FCSTD DOCUMENT  (FreeCAD 0.17R9910 (Git))
Label: housing
License: All rights reserved
LicenseURL: http://en.wikipedia.org/wiki/All_rights_reserved
objects: Sketcher::SketchObject×1, PartDesign::Body×1, App::Part×1
note: 2 computed .brp shape members not serialized (recipe doc carries the construction recipe); baked Part::Feature solids carry a one-line shape summary decoded from their .brp

FEATURE [Sketcher::SketchObject] Sketch
  MapMode = 5
  Support = -> [XY_Plane001]
  sketch-geometry (22):
    g0: LineSegment StartX=0 StartY=42 StartZ=0 EndX=26 EndY=42 EndZ=0
    g1: LineSegment StartX=26 StartY=42 StartZ=0 EndX=34 EndY=42 EndZ=0
    g2: LineSegment StartX=34 StartY=42 StartZ=0 EndX=34 EndY=50 EndZ=0
    g3: LineSegment StartX=34 StartY=50 StartZ=0 EndX=39 EndY=55 EndZ=0
    g4: LineSegment StartX=39 StartY=55 StartZ=0 EndX=55 EndY=55 EndZ=0
    g5: LineSegment StartX=55 StartY=55 StartZ=0 EndX=60 EndY=50 EndZ=0
    g6: LineSegment StartX=60 StartY=50 StartZ=0 EndX=60 EndY=42 EndZ=0
    g7: LineSegment StartX=60 StartY=42 StartZ=0 EndX=68 EndY=42 EndZ=0
    g8: LineSegment StartX=68 StartY=0 StartZ=0 EndX=60 EndY=0 EndZ=0
    g9: LineSegment StartX=60 StartY=0 StartZ=0 EndX=34 EndY=0 EndZ=0
    g10: LineSegment StartX=34 StartY=0 StartZ=0 EndX=26 EndY=0 EndZ=0
    g11: LineSegment StartX=26 StartY=0 StartZ=0 EndX=0 EndY=0 EndZ=0
    g12: LineSegment [constr] StartX=0 StartY=0 StartZ=0 EndX=0 EndY=42 EndZ=0
    g13: LineSegment [constr] StartX=34 StartY=42 StartZ=0 EndX=60 EndY=42 EndZ=0
    g14: LineSegment [constr] StartX=26 StartY=42 StartZ=0 EndX=26 EndY=0 EndZ=0
    g15: LineSegment [constr] StartX=34 StartY=0 StartZ=0 EndX=34 EndY=42 EndZ=0
    g16: LineSegment [constr] StartX=60 StartY=42 StartZ=0 EndX=60 EndY=0 EndZ=0
    g17: LineSegment [constr] StartX=34 StartY=50 StartZ=0 EndX=60 EndY=50 EndZ=0
    g18: LineSegment StartX=68 StartY=42 StartZ=0 EndX=68 EndY=0 EndZ=0
    g19: LineSegment StartX=0 StartY=42 StartZ=0 EndX=-5 EndY=37 EndZ=0
    g20: LineSegment StartX=-5 StartY=37 StartZ=0 EndX=-5 EndY=5 EndZ=0
    g21: LineSegment StartX=-5 StartY=5 StartZ=0 EndX=0 EndY=0 EndZ=0
  constraints (59):
    c: Horizontal(g0)
    c: Coincident(g0,g1)
    c: Horizontal(g1)
    c: Coincident(g1,g2)
    c: Vertical(g2)
    c: Coincident(g2,g3)
    c: Coincident(g3,g4)
    c: Horizontal(g4)
    c: Coincident(g4,g5)
    c: Coincident(g5,g6)
    c: Vertical(g6)
    c: Coincident(g6,g7)
    c: Coincident(g8,g9)
    c: Horizontal(g9)
    c: Coincident(g9,g10)
    c: Coincident(g10,g11)
    c: Horizontal(g11)
    c: Coincident(g11,g12)
    c: Coincident(g12,g0)
    c: Vertical(g12)
    c: Horizontal(g10)
    c: Horizontal(g8)
    c: Horizontal(g7)
    c: Coincident(g13,g1)
    c: Coincident(g13,g6)
    c: Coincident(g14,g0)
    c: Coincident(g14,g10)
    c: Vertical(g14)
    c: Coincident(g15,g9)
    c: Coincident(g15,g1)
    c: Vertical(g15)
    c: Coincident(g16,g6)
    c: Coincident(g16,g8)
    c: Vertical(g16)
    c: Equal(g11,g9)
    c: Equal(g10,g8)
    c: DistanceX(g11,g11) = 26
    c: DistanceX(g10,g10) = 8
    c: Equal(g3,g5)
    c: Angle(g2,g3) = 2.35619
    c: Coincident(g17,g2)
    c: Coincident(g17,g5)
    c: Horizontal(g17)
    c: Equal(g1,g2)
    c: Coincident(g11,g-1)
    c: DistanceY(g2,g3) = 5
    c: Coincident(g18,g7)
    c: Coincident(g18,g8)
    c: Horizontal(g13)
    c: DistanceY(g12,g12) = 42
    c: Vertical(g18)
    c: Coincident(g0,g19)
    c: Coincident(g19,g20)
    c: Vertical(g20)
    c: Coincident(g20,g21)
    c: Coincident(g21,g-1)
    c: Equal(g19,g21)
    c: DistanceX(g20,g-1) = 5
    c: Angle(g19,g12) = 0.785398
FEATURE [PartDesign::Body] Body
  Group = -> [Sketch]
  Origin = -> BodyOrigin
FEATURE [App::Part] Part
  Group = -> [Body]
  License = CC BY 3.0
  LicenseURL = http://creativecommons.org/licenses/by/3.0/
  Origin = -> PartOrigin
